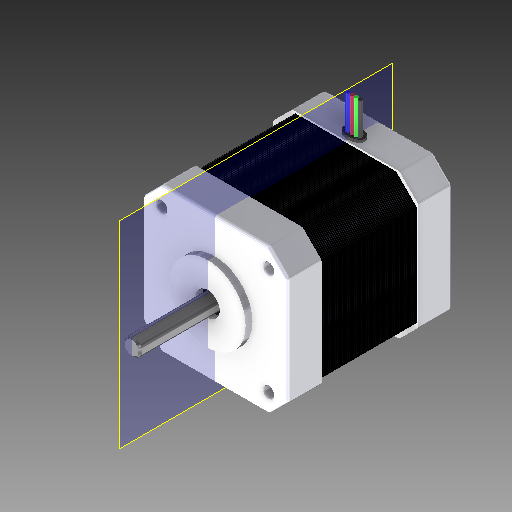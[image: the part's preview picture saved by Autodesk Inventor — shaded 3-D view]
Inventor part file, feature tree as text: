
AUTODESK INVENTOR PART (.ipt)
format: ipt  version: 2018 (Build 220112000, 112)  size: 1,114,112 bytes
history: native  units: mm
features: extrude x12, sketch x4, hole x4, fillet x4, plane x2, chamfer x2, pattern_linear x1, projected_geometry x1
ambient origin geometry x8: Origin, YZ Plane, XZ Plane, XY Plane, X Axis, Y Axis, Z Axis, Center Point
bodies: Solid1 (feature_tree)
feature tree (30):
  sketch  "Sketch1"  dims[d0=7.0mm d1=22.0mm]
  extrude  "Extrusion1"  Depth=22.0mm
  extrude  "Extrusion2"  Depth=31.0mm
  extrude  "Extrusion3"  Depth=3.0mm
  plane  "Work Plane2"
  extrude  "Extrusion7"  Depth=10.0mm
  extrude  "Extrusion8"  Depth=10.0mm
  chamfer  "Chamfer1"  Distance=42.0mm
  pattern_linear  "Rectangular Pattern2"  Spacing1=42.0mm  [1 undecoded]
  hole  "Hole1"  [1 undecoded]
  hole  "Hole2"  [1 undecoded]
  hole  "Hole3"  [1 undecoded]
  hole  "Hole4"  [1 undecoded]
  extrude  "Extrusion9"  Depth=10.0mm
  fillet  "Fillet1"  Radius=24.0mm
  fillet  "Fillet2"  Radius=2.0mm
  chamfer  "Chamfer2"  Distance=48.0mm
  fillet  "Fillet3"  [1 undecoded]
  sketch  "Sketch6"  dims[d10=3.0mm d11=3.0mm d12=3.0mm d39=42.0mm d40=42.0mm d41=135.0deg d42=51.618795mm d43=51.618795mm d44=25.809398mm d45=25.809398mm d46=24.0mm d47=0.0mm d48=2.0mm d49=0.0mm d50=48.0mm d51=0.0mm d60=-10.0mm d126=28.0mm d127=0.0mm d128=1.0mm d129=1.0mm d130=1.0mm d131=1.0mm d132=0.5mm d134=0.5mm d135=0.5mm d136=0.5mm d137=0.5mm d138=1.0mm d139=1.0mm d140=0.5mm d141=0.0mm d145=0.125mm d146=2.0mm d147=45.0deg d148=560.0mm d150=0.5mm d151=10.0mm d152=10.0mm d153=6.0mm d154=6.0mm d155=4.0mm d156=2.0mm d157=90.0deg d158=3.0mm d159=0.0mm d160=10.0mm d161=10.0mm d162=6.0mm d163=6.0mm d164=4.0mm d165=2.0mm d166=90.0deg d167=3.0mm d168=0.0mm d169=10.0mm d170=10.0mm d171=6.0mm d172=6.0mm d173=4.0mm d174=2.0mm d175=90.0deg d176=3.0mm d177=0.0mm d178=10.0mm d179=10.0mm d180=6.0mm d181=6.0mm d182=4.0mm d183=2.0mm d184=90.0deg d185=3.0mm d186=0.0mm d187=48.0mm d188=0.0mm d189=47.0mm d190=0.0mm d191=1.0mm d192=1.0mm d193=0.5mm d194=2.0mm d195=45.0deg d196=0.5mm d197=1.2mm d198=40.0mm d200=1.2mm d201=10.0mm d203=10.0mm d205=2.5mm d206=2.5mm d207=1.0mm d208=0.0mm d209=0.3mm d210=10.0mm d211=0.0mm d212=10.0mm d213=0.0mm d214=10.0mm d215=0.0mm d216=10.0mm d217=0.0mm d218=0.2mm d219=5.0mm d220=0.0mm d221=0.0mm]
  extrude  "Extrusion10"  Depth=10.0mm TaperAngle=0.0deg
  fillet  "Fillet4"  Radius=1.0mm
  extrude  "Extrusion11"  Depth=10.0mm
  extrude  "Extrusion12"  Depth=10.0mm
  extrude  "Extrusion13"  Depth=10.0mm
  extrude  "Extrusion14"  Depth=10.0mm
  extrude  "Extrusion15"  Depth=10.0mm
  plane  "Work Plane3"
  sketch  "Sketch4"  dims[d4=5.0mm d5=31.0mm]
  projected_geometry  "Projected Loop2"
  sketch  "Sketch5"  dims[d6=31.0mm d9=3.0mm]
note: 6 required parameter values undecoded (feature->parameter linkage not recoverable at this tier; creation-order binding heuristic only, values carry confidence <= 0.55)
